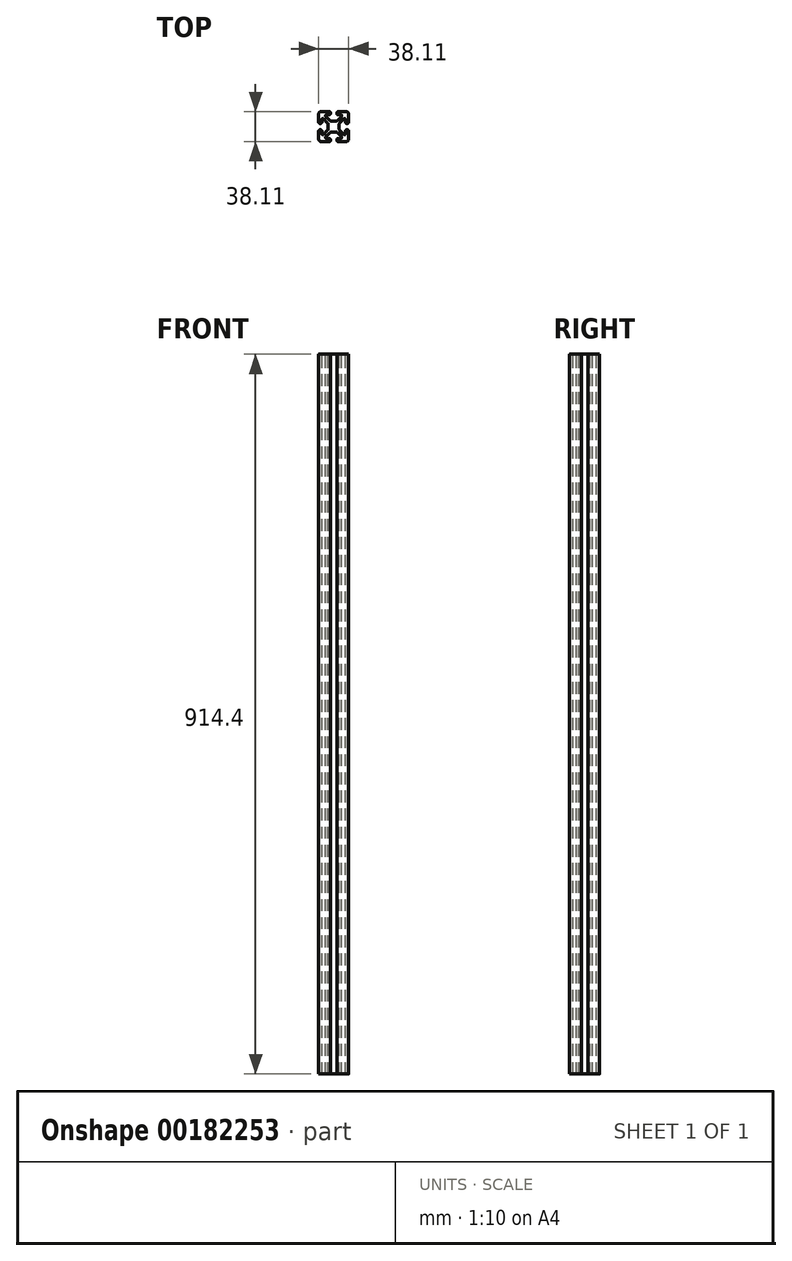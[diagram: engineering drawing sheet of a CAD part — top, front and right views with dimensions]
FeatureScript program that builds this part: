
annotation { "Feature Type Name" : "Feature", "Feature Type Description" : "" }
export const myFeature = defineFeature(function(context is Context, id is Id, definition is map)
    precondition{}
    {
        {
            var Q0;
            Q0=qCreatedBy(makeId("Top.planeOp"),FACE);
            var sketch = newSketch(context, id + "F0", { "sketchPlane" : qUnion([Q0])});
            skLineSegment(sketch, "E0.0", {"start": v(-3.18, 31.75) * mm, "end": v(-3.18, 21.51) * mm});
            skArc(sketch, "E1.0", {"start": v(0, 34.93) * mm, "mid": v(-2.25, 34) * mm, "end": v(-3.18, 31.75) * mm});
            skArc(sketch, "E2.0", {"start": v(-3.18, 21.51) * mm, "mid": v(-2.71, 20.4) * mm, "end": v(-1.6, 19.94) * mm});
            skLineSegment(sketch, "E3.0", {"start": v(-1.6, 19.94) * mm, "end": v(-0.69, 19.94) * mm});
            skArc(sketch, "E4.0", {"start": v(-0.69, 19.94) * mm, "mid": v(0.43, 20.4) * mm, "end": v(0.89, 21.51) * mm});
            skLineSegment(sketch, "E5.0", {"start": v(0.89, 21.51) * mm, "end": v(0.89, 25.27) * mm});
            skArc(sketch, "E6.0", {"start": v(0.89, 25.27) * mm, "mid": v(1.15, 25.9) * mm, "end": v(1.78, 26.16) * mm});
            skLineSegment(sketch, "E7.0", {"start": v(1.78, 26.16) * mm, "end": v(2.35, 26.16) * mm});
            skArc(sketch, "E8.0", {"start": v(2.35, 26.16) * mm, "mid": v(2.69, 26.1) * mm, "end": v(2.97, 25.9) * mm});
            skLineSegment(sketch, "E9.0", {"start": v(2.97, 25.9) * mm, "end": v(7.61, 21.26) * mm});
            skArc(sketch, "E10.0", {"start": v(7.61, 21.26) * mm, "mid": v(8.64, 19.72) * mm, "end": v(9, 17.9) * mm});
            skLineSegment(sketch, "E11.0", {"start": v(9, 17.9) * mm, "end": v(9, 13.85) * mm});
            skArc(sketch, "E12.0", {"start": v(9, 13.85) * mm, "mid": v(8.64, 12.03) * mm, "end": v(7.61, 10.49) * mm});
            skLineSegment(sketch, "E13.0", {"start": v(7.61, 10.49) * mm, "end": v(2.97, 5.85) * mm});
            skArc(sketch, "E14.0", {"start": v(2.97, 5.85) * mm, "mid": v(2.69, 5.66) * mm, "end": v(2.35, 5.59) * mm});
            skLineSegment(sketch, "E15.0", {"start": v(2.35, 5.59) * mm, "end": v(1.78, 5.59) * mm});
            skArc(sketch, "E16.0", {"start": v(1.78, 5.59) * mm, "mid": v(1.15, 5.85) * mm, "end": v(0.89, 6.48) * mm});
            skLineSegment(sketch, "E17.0", {"start": v(0.89, 6.48) * mm, "end": v(0.89, 10.24) * mm});
            skArc(sketch, "E18.0", {"start": v(0.89, 10.24) * mm, "mid": v(0.43, 11.35) * mm, "end": v(-0.69, 11.81) * mm});
            skLineSegment(sketch, "E19.0", {"start": v(-0.69, 11.81) * mm, "end": v(-1.6, 11.81) * mm});
            skArc(sketch, "E20.0", {"start": v(-1.6, 11.81) * mm, "mid": v(-2.71, 11.35) * mm, "end": v(-3.17, 10.24) * mm});
            skLineSegment(sketch, "E21.0", {"start": v(-3.17, 10.24) * mm, "end": v(-3.17, 0) * mm});
            skArc(sketch, "E22.0", {"start": v(-3.17, 0) * mm, "mid": v(-2.25, -2.25) * mm, "end": v(0, -3.17) * mm});
            skLineSegment(sketch, "E23.0", {"start": v(0, -3.17) * mm, "end": v(10.24, -3.17) * mm});
            skArc(sketch, "E24.0", {"start": v(10.24, -3.17) * mm, "mid": v(11.35, -2.71) * mm, "end": v(11.81, -1.6) * mm});
            skLineSegment(sketch, "E25.0", {"start": v(11.81, -1.6) * mm, "end": v(11.81, -0.69) * mm});
            skArc(sketch, "E26.0", {"start": v(11.81, -0.69) * mm, "mid": v(11.35, 0.43) * mm, "end": v(10.24, 0.89) * mm});
            skLineSegment(sketch, "E27.0", {"start": v(10.24, 0.89) * mm, "end": v(6.48, 0.89) * mm});
            skArc(sketch, "E28.0", {"start": v(6.48, 0.89) * mm, "mid": v(5.85, 1.15) * mm, "end": v(5.59, 1.78) * mm});
            skLineSegment(sketch, "E29.0", {"start": v(5.59, 1.78) * mm, "end": v(5.59, 2.35) * mm});
            skArc(sketch, "E30.0", {"start": v(5.59, 2.35) * mm, "mid": v(5.66, 2.69) * mm, "end": v(5.85, 2.97) * mm});
            skLineSegment(sketch, "E31.0", {"start": v(5.85, 2.97) * mm, "end": v(10.49, 7.61) * mm});
            skArc(sketch, "E32.0", {"start": v(10.49, 7.61) * mm, "mid": v(12.03, 8.64) * mm, "end": v(13.85, 9) * mm});
            skLineSegment(sketch, "E33.0", {"start": v(13.85, 9) * mm, "end": v(17.9, 9) * mm});
            skArc(sketch, "E34.0", {"start": v(17.9, 9) * mm, "mid": v(19.72, 8.64) * mm, "end": v(21.26, 7.61) * mm});
            skLineSegment(sketch, "E35.0", {"start": v(21.26, 7.61) * mm, "end": v(25.9, 2.97) * mm});
            skArc(sketch, "E36.0", {"start": v(25.9, 2.97) * mm, "mid": v(26.1, 2.69) * mm, "end": v(26.16, 2.35) * mm});
            skPoint(sketch, "E37.0", {"position": v(26.16, 1.78) * mm});
            skArc(sketch, "E38.0", {"start": v(26.16, 1.78) * mm, "mid": v(25.9, 1.15) * mm, "end": v(25.27, 0.89) * mm});
            skLineSegment(sketch, "E39.0", {"start": v(25.27, 0.89) * mm, "end": v(21.51, 0.89) * mm});
            skArc(sketch, "E40.0", {"start": v(21.51, 0.89) * mm, "mid": v(20.4, 0.43) * mm, "end": v(19.94, -0.69) * mm});
            skPoint(sketch, "E41.0", {"position": v(19.94, -1.6) * mm});
            skLineSegment(sketch, "E42.0", {"start": v(19.94, -0.69) * mm, "end": v(19.94, -1.6) * mm});
            skArc(sketch, "E43.0", {"start": v(19.94, -1.6) * mm, "mid": v(20.4, -2.71) * mm, "end": v(21.51, -3.17) * mm});
            skLineSegment(sketch, "E44.0", {"start": v(21.51, -3.17) * mm, "end": v(31.75, -3.17) * mm});
            skArc(sketch, "E45.0", {"start": v(31.75, -3.17) * mm, "mid": v(34, -2.25) * mm, "end": v(34.93, 0) * mm});
            skLineSegment(sketch, "E46.0", {"start": v(34.93, 0) * mm, "end": v(34.93, 10.24) * mm});
            skArc(sketch, "E47.0", {"start": v(34.93, 10.24) * mm, "mid": v(34.46, 11.35) * mm, "end": v(33.35, 11.81) * mm});
            skLineSegment(sketch, "E48.0", {"start": v(33.35, 11.81) * mm, "end": v(32.44, 11.81) * mm});
            skArc(sketch, "E49.0", {"start": v(32.44, 11.81) * mm, "mid": v(31.32, 11.35) * mm, "end": v(30.86, 10.24) * mm});
            skLineSegment(sketch, "E50.0", {"start": v(30.86, 10.24) * mm, "end": v(30.86, 6.48) * mm});
            skArc(sketch, "E51.0", {"start": v(30.86, 6.48) * mm, "mid": v(30.6, 5.85) * mm, "end": v(29.97, 5.59) * mm});
            skLineSegment(sketch, "E52.0", {"start": v(29.97, 5.59) * mm, "end": v(29.4, 5.59) * mm});
            skArc(sketch, "E53.0", {"start": v(29.4, 5.59) * mm, "mid": v(29.06, 5.66) * mm, "end": v(28.78, 5.85) * mm});
            skLineSegment(sketch, "E54.0", {"start": v(28.78, 5.85) * mm, "end": v(24.14, 10.49) * mm});
            skArc(sketch, "E55.0", {"start": v(24.14, 10.49) * mm, "mid": v(23.1, 12.03) * mm, "end": v(22.74, 13.85) * mm});
            skLineSegment(sketch, "E56.0", {"start": v(22.74, 13.85) * mm, "end": v(22.74, 17.9) * mm});
            skArc(sketch, "E57.0", {"start": v(22.74, 17.9) * mm, "mid": v(23.1, 19.72) * mm, "end": v(24.14, 21.26) * mm});
            skLineSegment(sketch, "E58.0", {"start": v(24.14, 21.26) * mm, "end": v(28.78, 25.9) * mm});
            skArc(sketch, "E59.0", {"start": v(28.78, 25.9) * mm, "mid": v(29.06, 26.1) * mm, "end": v(29.4, 26.16) * mm});
            skLineSegment(sketch, "E60.0", {"start": v(29.4, 26.16) * mm, "end": v(29.97, 26.16) * mm});
            skArc(sketch, "E61.0", {"start": v(29.97, 26.16) * mm, "mid": v(30.6, 25.9) * mm, "end": v(30.86, 25.27) * mm});
            skLineSegment(sketch, "E62.0", {"start": v(30.86, 25.27) * mm, "end": v(30.86, 21.51) * mm});
            skArc(sketch, "E63.0", {"start": v(30.86, 21.51) * mm, "mid": v(31.32, 20.4) * mm, "end": v(32.44, 19.94) * mm});
            skLineSegment(sketch, "E64.0", {"start": v(32.44, 19.94) * mm, "end": v(33.35, 19.94) * mm});
            skArc(sketch, "E65.0", {"start": v(33.35, 19.94) * mm, "mid": v(34.46, 20.4) * mm, "end": v(34.93, 21.51) * mm});
            skLineSegment(sketch, "E66.0", {"start": v(34.93, 21.51) * mm, "end": v(34.93, 31.75) * mm});
            skArc(sketch, "E67.0", {"start": v(34.93, 31.75) * mm, "mid": v(34, 34) * mm, "end": v(31.75, 34.93) * mm});
            skLineSegment(sketch, "E68.0", {"start": v(31.75, 34.93) * mm, "end": v(21.51, 34.93) * mm});
            skArc(sketch, "E69.0", {"start": v(21.51, 34.93) * mm, "mid": v(20.4, 34.46) * mm, "end": v(19.94, 33.35) * mm});
            skLineSegment(sketch, "E70.0", {"start": v(19.94, 33.35) * mm, "end": v(19.94, 32.44) * mm});
            skArc(sketch, "E71.0", {"start": v(19.94, 32.44) * mm, "mid": v(20.4, 31.32) * mm, "end": v(21.51, 30.86) * mm});
            skLineSegment(sketch, "E72.0", {"start": v(21.51, 30.86) * mm, "end": v(25.27, 30.86) * mm});
            skArc(sketch, "E73.0", {"start": v(25.27, 30.86) * mm, "mid": v(25.9, 30.6) * mm, "end": v(26.16, 29.97) * mm});
            skLineSegment(sketch, "E74.0", {"start": v(26.16, 29.97) * mm, "end": v(26.16, 29.4) * mm});
            skArc(sketch, "E75.0", {"start": v(26.16, 29.4) * mm, "mid": v(26.1, 29.06) * mm, "end": v(25.9, 28.78) * mm});
            skLineSegment(sketch, "E76.0", {"start": v(25.9, 28.78) * mm, "end": v(21.26, 24.14) * mm});
            skArc(sketch, "E77.0", {"start": v(11.81, 33.35) * mm, "mid": v(11.35, 34.46) * mm, "end": v(10.24, 34.93) * mm});
            skLineSegment(sketch, "E78.0", {"start": v(11.81, 32.44) * mm, "end": v(11.81, 33.35) * mm});
            skArc(sketch, "E79.0", {"start": v(10.24, 30.86) * mm, "mid": v(11.35, 31.32) * mm, "end": v(11.81, 32.44) * mm});
            skLineSegment(sketch, "E80.0", {"start": v(6.48, 30.86) * mm, "end": v(10.24, 30.86) * mm});
            skArc(sketch, "E81.0", {"start": v(5.59, 29.97) * mm, "mid": v(5.85, 30.6) * mm, "end": v(6.48, 30.86) * mm});
            skLineSegment(sketch, "E82.0", {"start": v(5.59, 29.4) * mm, "end": v(5.59, 29.97) * mm});
            skArc(sketch, "E83.0", {"start": v(5.85, 28.78) * mm, "mid": v(5.66, 29.06) * mm, "end": v(5.59, 29.4) * mm});
            skLineSegment(sketch, "E84.0", {"start": v(10.49, 24.14) * mm, "end": v(5.85, 28.78) * mm});
            skArc(sketch, "E85.0", {"start": v(13.85, 22.74) * mm, "mid": v(12.03, 23.1) * mm, "end": v(10.49, 24.14) * mm});
            skLineSegment(sketch, "E86.0", {"start": v(17.9, 22.74) * mm, "end": v(13.85, 22.74) * mm});
            skArc(sketch, "E87.0", {"start": v(21.26, 24.14) * mm, "mid": v(19.72, 23.1) * mm, "end": v(17.9, 22.74) * mm});
            skLineSegment(sketch, "E88.0", {"start": v(26.16, 2.35) * mm, "end": v(26.16, 1.78) * mm});
            skLineSegment(sketch, "E89", {"start": v(0, 34.93) * mm, "end": v(10.24, 34.93) * mm});
            skSolve(sketch);
        }
        {
            var Q0;
            Q0=qSketchRegion(id+"F0",true);
            extrude(context, id + "F1", {"entities" : qUnion([Q0]), "oppositeDirection" : true, "depth" : 914.4 * mm});
        }
    });
